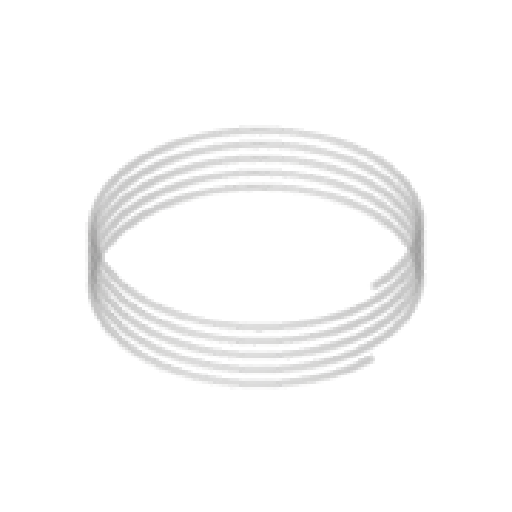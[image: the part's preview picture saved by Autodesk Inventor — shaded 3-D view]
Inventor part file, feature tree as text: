
AUTODESK INVENTOR PART (.ipt)
format: ipt  version: 2024.1 (Build 281209000, 209)  size: 318,464 bytes
history: native  units: mm
features: other x1, sketch x1
ambient origin geometry x8: Origin, YZ Plane, XZ Plane, XY Plane, X Axis, Y Axis, Z Axis, Center Point
bodies: Volumenkörper1 (feature_tree)
feature tree (2):
  other  "Spirale1"
  sketch  "Skizze1"  dims[d0=3.0mm d1=5.0mm d2=10.0mm d3=10.0mm d4=50.0mm d5=0.0mm d6=90.0deg d7=90.0deg d8=0.0mm d9=0.0mm]
